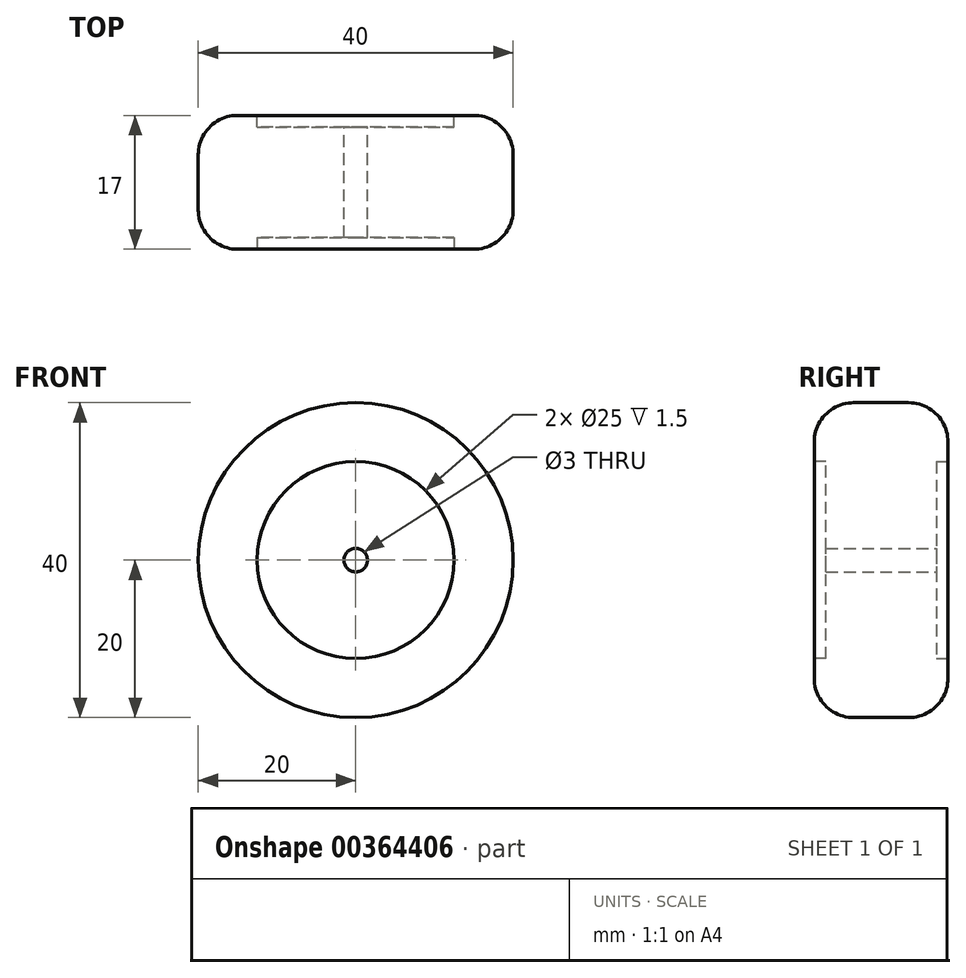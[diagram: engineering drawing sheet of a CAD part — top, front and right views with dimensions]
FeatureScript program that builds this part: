
annotation { "Feature Type Name" : "Feature", "Feature Type Description" : "" }
export const myFeature = defineFeature(function(context is Context, id is Id, definition is map)
    precondition{}
    {
        {
            var Q0;
            Q0=qCreatedBy(makeId("Front.planeOp"),FACE);
            var sketch = newSketch(context, id + "F0", { "sketchPlane" : qUnion([Q0])});
            skCircle(sketch, "E0", {"center": v(0, 0) * mm, "radius": 20 * mm});
            skCircle(sketch, "E1", {"center": v(0, 0) * mm, "radius": 1.5 * mm});
            skSolve(sketch);
        }
        {
            var Q0;
            Q0=makeQuery(id+"F0.imprint","IMPRINT",FACE,{"disambiguationData":[TD([[makeQuery(id+"F0.imprint","IMPRINT",EDGE,{"derivedFrom":sQuery(id+"F0.wireOp",EDGE,"E0")}),1.0]])]});
            extrude(context, id + "F1", {"entities" : qUnion([Q0]), "depth" : 17 * mm});
        }
        {
            var Q0;
            Q0=makeQuery(id+"F1.opExtrude","CAP_FACE",FACE,{"disambiguationData":[OSD([sQuery(id+"F0.wireOp",EDGE,"E0"),sQuery(id+"F0.wireOp",EDGE,"E1")])],"isStart":true});
            var sketch = newSketch(context, id + "F2", { "sketchPlane" : qUnion([Q0])});
            skCircle(sketch, "E2", {"center": v(0, 0) * mm, "radius": 12.5 * mm});
            skSolve(sketch);
        }
        {
            var Q0;
            Q0 = qSketchRegion(id + "F2", true);
            extrude(context, id + "F3", {"entities" : qUnion([Q0]), "operationType" : NewBodyOperationType.REMOVE, "oppositeDirection" : true, "depth" : 1.5 * mm});
        }
        {
            var Q0;
            Q0=makeQuery(id+"F1.opExtrude","CAP_FACE",FACE,{"disambiguationData":[OSD([sQuery(id+"F0.wireOp",EDGE,"E0"),sQuery(id+"F0.wireOp",EDGE,"E1")])],"isStart":false});
            var sketch = newSketch(context, id + "F4", { "sketchPlane" : qUnion([Q0])});
            skCircle(sketch, "E3", {"center": v(0, 0) * mm, "radius": 12.5 * mm});
            skSolve(sketch);
        }
        {
            var Q0;
            Q0=makeQuery(id+"F4.imprint","IMPRINT",FACE,{"disambiguationData":[TD([[makeQuery(id+"F4.imprint","IMPRINT",EDGE,{"derivedFrom":sQuery(id+"F4.wireOp",EDGE,"E3")}),1.0]])]});
            extrude(context, id + "F5", {"entities" : qUnion([Q0]), "operationType" : NewBodyOperationType.REMOVE, "oppositeDirection" : true, "depth" : 1.5 * mm});
        }
        {
            var Q0;
            Q0=makeQuery(id+"F1.opExtrude","CAP_EDGE",EDGE,{"disambiguationData":[OSD([sQuery(id+"F0.wireOp",EDGE,"E0")])],"isStart":true});
            var Q1;
            Q1=makeQuery(id+"F1.opExtrude","CAP_EDGE",EDGE,{"disambiguationData":[OSD([sQuery(id+"F0.wireOp",EDGE,"E0")])],"isStart":false});
            fillet(context, id + "F6", {"entities" : qUnion([Q0, Q1]), "radius" : 5 * mm, "tangentPropagation" : true, "allowEdgeOverflow" : false});
        }
    });
